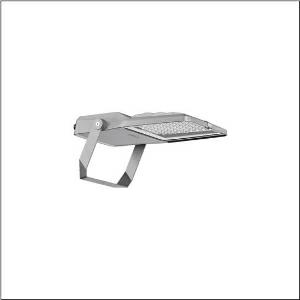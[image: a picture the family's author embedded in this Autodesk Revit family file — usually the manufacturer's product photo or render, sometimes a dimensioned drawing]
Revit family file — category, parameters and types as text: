
# Revit family: floodlight_fl_21_mini___pl52_5xa7775d2d1a_5239
name_source: partatom
category: Lighting Fixtures
units: mm (PartAtom-declared; Revit-internal decimal feet)

## family parameters
Cut with Voids When Loaded = No
Host = Face
Light Source = No
Part Type = Normal
Room Calculation Point = No
Round Connector Dimension = Use Diameter
Shared = No

## types (1)
- --- (1 x LED, 17840 lm, 142.9 W, 3000K)
    Apparent Load = 143 VA
    CIE Flux Codes = 26 60 98 100 100
    Color Rendering = 70
    Color Temperature = 3000K
    Default Elevation = 1800 mm
    Description = Floodlight FL 21 mini, floodlight, primary light control with lens, of PMMA, primary optical cover: protective disc, of toughened safety glass, transparent, light distribution: PL52, light emission: direct distribution, installation type: surface-mounted, LED, High Power LED, rated luminous flux: 17.840lm, luminous efficacy: 125lm/W, light colour: 730, colour temperature: 3000K, control gear: Smart Interface (Zhaga), control: flexible luminous flux parameterisation, time-dependent luminous flux control, constant luminous flux control, overheat protection, pre-setting: logarithmic dimming characteristic, with terminal, 6-pole, mains connection: 220..240V, AC, 50/60Hz, start of lifetime: 143W, end of service life: 151W, reduction: 63W, luminaire housing, of diecast aluminium, powder-coated, Siteco® metallic grey (DB 702S), corrosivity category C5 mid according to DIN EN ISO 12944, suitable for swimming pools, chlorine-resistant, sealing non-destructively replaceable, mounting bracket, of steel, galvanised, powder-coated, Siteco® metallic grey (DB 702S), Smart Interface above, protection rating (complete): IP66, insulation class (complete): insulation class II (safety insulation), certification: CE, ENEC, VDE, protection symbol: D, impact resistance: IK08, permissible operating ambient temperature: -40..+40°C, permissible operating ambient temperature for outdoor applications: -40..+50°C, standard: DIN EN 12944, LABS conformity tested according to VDMA 24364:2018-05, packaging unit: 1 piece

Light Distribution: PL52
    Height = 70 mm
    Lamp = 1 x LED
    Lamp Light Flux = 17840 lm
    Lamp Power = 142.9 W
    Lamp count = 1
    Length = 485 mm
    Luminous efficacy = 125 lm/W
    Manufacturer = Siteco
    ModVariant = No
    Model = 5XA7775D2D1A
    Number of Poles = 1
    OnlyDefault = Yes
    Power Factor = 1
    Product Name = Floodlight FL 21 mini | PL52
    Product group = floodlight | pylon annexe
    ProductGroupID = 6200
    Protection Class = Protection class II
    Protection Degree = IP 66
    RLX_Detail_Level = 1
    RLX_Emergency_Light_Flux = 0 lm
    RLX_Emergency_Type = 0
    RLX_Emergency_Type_DB = No
    RlxData = <blob elided: 96489 chars, md5=b121986c>
    Socket = socket
    Standby Power = 0 W
    System Light Flux = 17840 lm
    System Power = 143 W
    Type Comments = factory setting: luminous flux: 100 % | dim-lin: 254 | 730 mA
    Type Image = l_1006845.jpg
    URL = http://relux.com
    VarID = @adj_163222
    Voltage = 0 V
    Weight = 0.00 kg
    Width = 337 mm

## geometry (parser evidence)
native form markers: Blend x4, Sweep x12
no freeform markers — native parametric forms only
